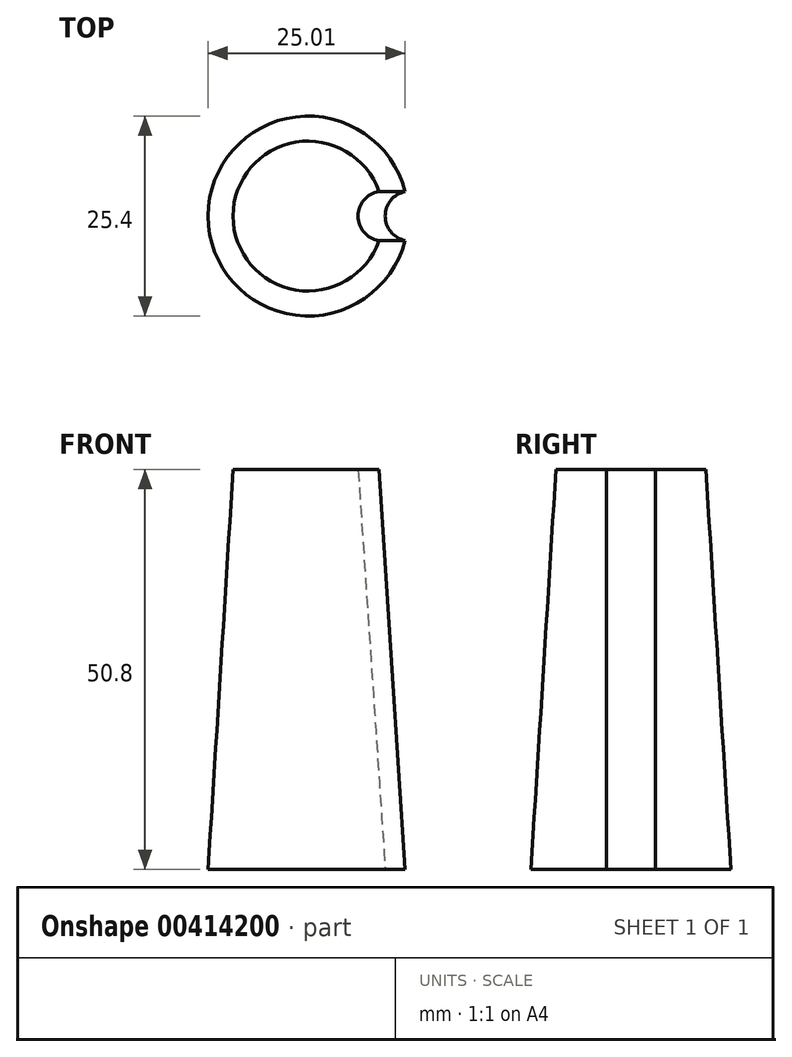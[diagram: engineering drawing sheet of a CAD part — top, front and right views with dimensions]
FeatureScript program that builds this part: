
annotation { "Feature Type Name" : "Feature", "Feature Type Description" : "" }
export const myFeature = defineFeature(function(context is Context, id is Id, definition is map)
    precondition{}
    {
        {
            var Q0;
            Q0=qCreatedBy(makeId("Top.planeOp"),FACE);
            var sketch = newSketch(context, id + "F0", { "sketchPlane" : qUnion([Q0])});
            skArc(sketch, "E0", {"start": v(12.31, 3.1) * mm, "mid": v(-12.7, 0) * mm, "end": v(12.31, -3.1) * mm});
            skLineSegment(sketch, "E1", {"start": v(0, 0) * mm, "end": v(25.95, 0) * mm, "construction": true});
            skArc(sketch, "E2", {"start": v(12.31, 3.1) * mm, "mid": v(9.8, 0) * mm, "end": v(12.31, -3.1) * mm});
            skSolve(sketch);
        }
        {
            var Q0;
            Q0=qCreatedBy(makeId("Top.planeOp"),FACE);
            cPlane(context, id + "F1", {"entities" : qUnion([Q0]), "cplaneType" : CPlaneType.OFFSET, "offset" : 50.8 * mm, "width" : 152.4 * mm, "height" : 152.4 * mm});
        }
        {
            var Q0;
            Q0=qCreatedBy(id+"F1.planeOp",FACE);
            var sketch = newSketch(context, id + "F2", { "sketchPlane" : qUnion([Q0])});
            skArc(sketch, "E3", {"start": v(9, 3.13) * mm, "mid": v(-9.52, 0) * mm, "end": v(9, -3.13) * mm});
            skLineSegment(sketch, "E4", {"start": v(0, 0) * mm, "end": v(26.18, 0) * mm, "construction": true});
            skArc(sketch, "E5", {"start": v(9, 3.13) * mm, "mid": v(6.35, 0) * mm, "end": v(9, -3.13) * mm});
            skSolve(sketch);
        }
        {
            var Q0;
            Q0=makeQuery(id+"F0.imprint","IMPRINT",FACE,{"disambiguationData":[TD([[makeQuery(id+"F0.imprint","IMPRINT",EDGE,{"derivedFrom":sQuery(id+"F0.wireOp",EDGE,"E0")}),1.0]])]});
            var Q1;
            Q1=makeQuery(id+"F2.imprint","IMPRINT",FACE,{"disambiguationData":[TD([[makeQuery(id+"F2.imprint","IMPRINT",EDGE,{"derivedFrom":sQuery(id+"F2.wireOp",EDGE,"E3")}),1.0]])]});
            loft(context, id + "F3", {"sheetProfilesArray" : [{ "sheetProfileEntities" : qUnion([Q0]) }, { "sheetProfileEntities" : qUnion([Q1]) }]});
        }
    });
